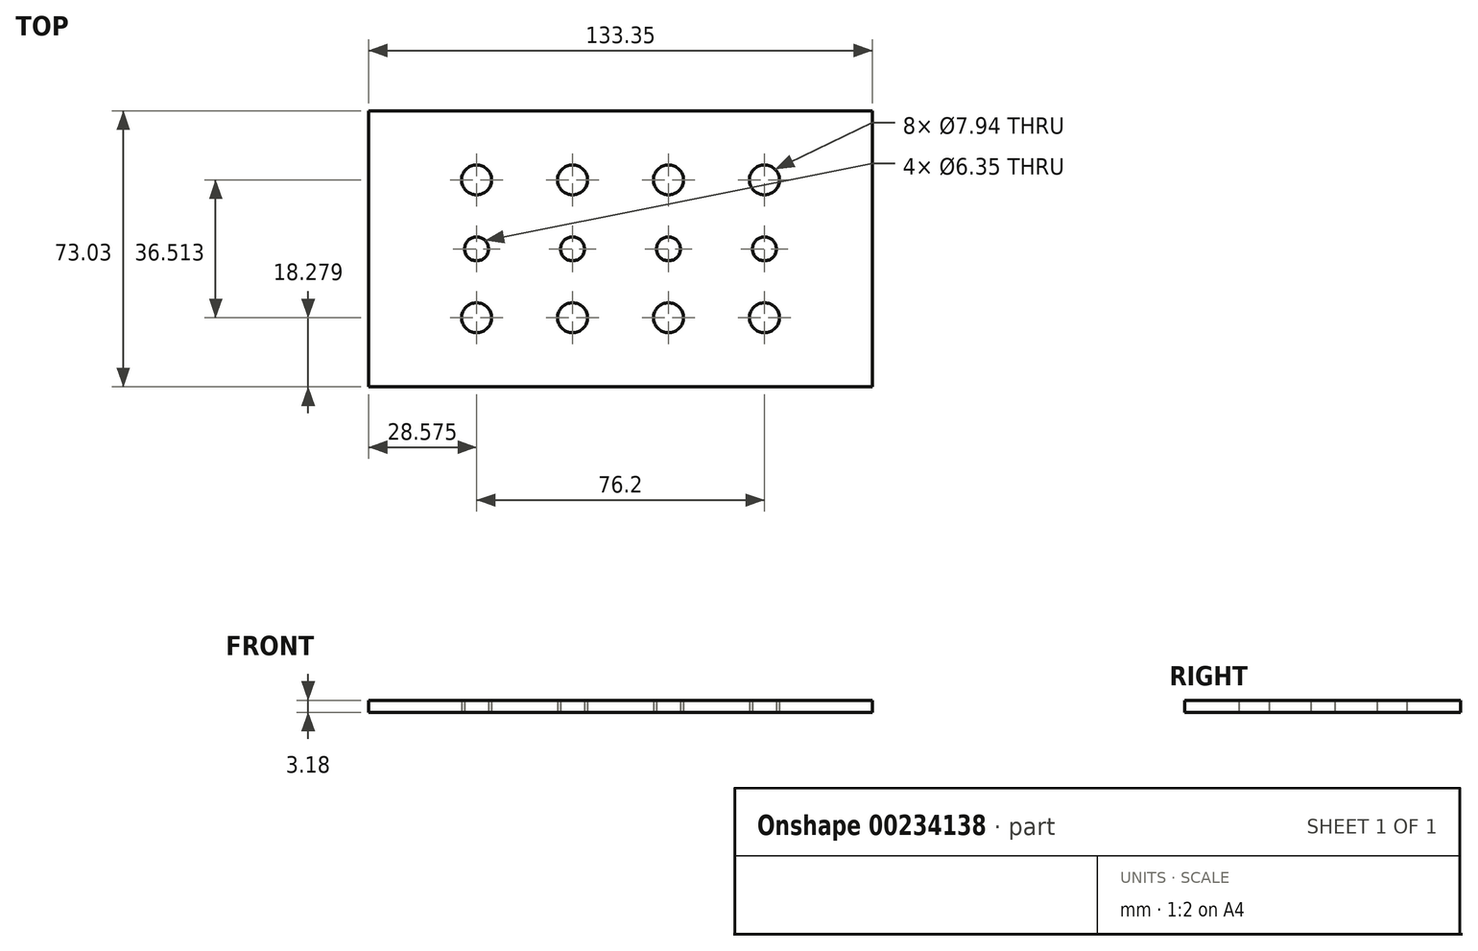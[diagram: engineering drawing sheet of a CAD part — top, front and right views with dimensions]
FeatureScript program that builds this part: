
annotation { "Feature Type Name" : "Feature", "Feature Type Description" : "" }
export const myFeature = defineFeature(function(context is Context, id is Id, definition is map)
    precondition{}
    {
        {
            var Q0;
            Q0=qCreatedBy(makeId("Top.planeOp"),FACE);
            var sketch = newSketch(context, id + "F0", { "sketchPlane" : qUnion([Q0])});
            skLineSegment(sketch, "E0.bottom", {"start": v(0, 0) * mm, "end": v(133.35, 0) * mm});
            skLineSegment(sketch, "E0.top", {"start": v(0, 73.03) * mm, "end": v(133.35, 73.03) * mm});
            skLineSegment(sketch, "E0.left", {"start": v(0, 0) * mm, "end": v(0, 73.03) * mm});
            skLineSegment(sketch, "E0.right", {"start": v(133.35, 0) * mm, "end": v(133.35, 73.03) * mm});
            skSolve(sketch);
        }
        {
            var Q0;
            Q0=makeQuery(id+"F0.imprint","IMPRINT",FACE,{"disambiguationData":[TD([[makeQuery(id+"F0.imprint","IMPRINT",EDGE,{"derivedFrom":sQuery(id+"F0.wireOp",EDGE,"E0.bottom")}),1.0]])]});
            extrude(context, id + "F1", {"entities" : qUnion([Q0]), "oppositeDirection" : true, "depth" : 3.17 * mm});
        }
        {
            var Q0;
            Q0=makeQuery(id+"F1.opExtrude","CAP_FACE",FACE,{"disambiguationData":[OSD([sQuery(id+"F0.wireOp",EDGE,"E0.bottom"),sQuery(id+"F0.wireOp",EDGE,"E0.top"),sQuery(id+"F0.wireOp",EDGE,"E0.left"),sQuery(id+"F0.wireOp",EDGE,"E0.right")])],"isStart":false});
            var sketch = newSketch(context, id + "F2", { "sketchPlane" : qUnion([Q0])});
            skLineSegment(sketch, "E1", {"start": v(0, -36.51) * mm, "end": v(133.35, -36.51) * mm, "construction": true});
            skCircle(sketch, "E2", {"center": v(28.58, -36.51) * mm, "radius": 3.18 * mm});
            skCircle(sketch, "E3.1.0.0", {"center": v(53.98, -36.51) * mm, "radius": 3.18 * mm});
            skCircle(sketch, "E3.2.0.0", {"center": v(79.38, -36.51) * mm, "radius": 3.18 * mm});
            skCircle(sketch, "E3.3.0.0", {"center": v(104.77, -36.51) * mm, "radius": 3.18 * mm});
            skLineSegment(sketch, "E3.direction1", {"start": v(28.58, -36.51) * mm, "end": v(53.98, -36.51) * mm, "construction": true});
            skSolve(sketch);
        }
        {
            var Q0;
            Q0=makeQuery(id+"F2.imprint","IMPRINT",FACE,{"disambiguationData":[TD([[makeQuery(id+"F2.imprint","IMPRINT",EDGE,{"derivedFrom":sQuery(id+"F2.wireOp",EDGE,"E2")}),1.0]])]});
            var Q1;
            Q1=makeQuery(id+"F2.imprint","IMPRINT",FACE,{"disambiguationData":[TD([[makeQuery(id+"F2.imprint","IMPRINT",EDGE,{"derivedFrom":sQuery(id+"F2.wireOp",EDGE,"E3.1.0.0")}),1.0]])]});
            var Q2;
            Q2=makeQuery(id+"F2.imprint","IMPRINT",FACE,{"disambiguationData":[TD([[makeQuery(id+"F2.imprint","IMPRINT",EDGE,{"derivedFrom":sQuery(id+"F2.wireOp",EDGE,"E3.2.0.0")}),1.0]])]});
            var Q3;
            Q3=makeQuery(id+"F2.imprint","IMPRINT",FACE,{"disambiguationData":[TD([[makeQuery(id+"F2.imprint","IMPRINT",EDGE,{"derivedFrom":sQuery(id+"F2.wireOp",EDGE,"E3.3.0.0")}),1.0]])]});
            extrude(context, id + "F3", {"entities" : qUnion([Q0, Q1, Q2, Q3]), "operationType" : NewBodyOperationType.REMOVE, "endBound" : BoundingType.THROUGH_ALL, "oppositeDirection" : true, "depth" : 25.4 * mm});
        }
        {
            var Q0;
            Q0=makeQuery(id+"F1.opExtrude","CAP_FACE",FACE,{"disambiguationData":[OSD([sQuery(id+"F0.wireOp",EDGE,"E0.bottom"),sQuery(id+"F0.wireOp",EDGE,"E0.top"),sQuery(id+"F0.wireOp",EDGE,"E0.left"),sQuery(id+"F0.wireOp",EDGE,"E0.right")])],"isStart":false});
            var sketch = newSketch(context, id + "F4", { "sketchPlane" : qUnion([Q0])});
            skLineSegment(sketch, "E4", {"start": v(0, -54.8) * mm, "end": v(125.38, -54.8) * mm, "construction": true});
            skCircle(sketch, "E5", {"center": v(28.58, -54.8) * mm, "radius": 3.97 * mm});
            skCircle(sketch, "E6.0.1.0", {"center": v(28.58, -18.28) * mm, "radius": 3.97 * mm});
            skCircle(sketch, "E6.1.0.0", {"center": v(53.98, -54.8) * mm, "radius": 3.97 * mm});
            skCircle(sketch, "E6.1.1.0", {"center": v(53.98, -18.28) * mm, "radius": 3.97 * mm});
            skCircle(sketch, "E6.2.0.0", {"center": v(79.38, -54.8) * mm, "radius": 3.97 * mm});
            skCircle(sketch, "E6.2.1.0", {"center": v(79.38, -18.28) * mm, "radius": 3.97 * mm});
            skCircle(sketch, "E6.3.0.0", {"center": v(104.77, -54.8) * mm, "radius": 3.97 * mm});
            skCircle(sketch, "E6.3.1.0", {"center": v(104.77, -18.28) * mm, "radius": 3.97 * mm});
            skLineSegment(sketch, "E6.direction1", {"start": v(28.58, -54.8) * mm, "end": v(53.98, -54.8) * mm, "construction": true});
            skLineSegment(sketch, "E6.direction2", {"start": v(28.58, -54.8) * mm, "end": v(28.58, -18.28) * mm, "construction": true});
            skSolve(sketch);
        }
        {
            var Q0;
            Q0=makeQuery(id+"F4.imprint","IMPRINT",FACE,{"disambiguationData":[TD([[makeQuery(id+"F4.imprint","IMPRINT",EDGE,{"derivedFrom":sQuery(id+"F4.wireOp",EDGE,"E5")}),1.0]])]});
            var Q1;
            Q1=makeQuery(id+"F4.imprint","IMPRINT",FACE,{"disambiguationData":[TD([[makeQuery(id+"F4.imprint","IMPRINT",EDGE,{"derivedFrom":sQuery(id+"F4.wireOp",EDGE,"E6.1.0.0")}),1.0]])]});
            var Q2;
            Q2=makeQuery(id+"F4.imprint","IMPRINT",FACE,{"disambiguationData":[TD([[makeQuery(id+"F4.imprint","IMPRINT",EDGE,{"derivedFrom":sQuery(id+"F4.wireOp",EDGE,"E6.2.0.0")}),1.0]])]});
            var Q3;
            Q3=makeQuery(id+"F4.imprint","IMPRINT",FACE,{"disambiguationData":[TD([[makeQuery(id+"F4.imprint","IMPRINT",EDGE,{"derivedFrom":sQuery(id+"F4.wireOp",EDGE,"E6.3.0.0")}),1.0]])]});
            var Q4;
            Q4=makeQuery(id+"F4.imprint","IMPRINT",FACE,{"disambiguationData":[TD([[makeQuery(id+"F4.imprint","IMPRINT",EDGE,{"derivedFrom":sQuery(id+"F4.wireOp",EDGE,"E6.3.1.0")}),1.0]])]});
            var Q5;
            Q5=makeQuery(id+"F4.imprint","IMPRINT",FACE,{"disambiguationData":[TD([[makeQuery(id+"F4.imprint","IMPRINT",EDGE,{"derivedFrom":sQuery(id+"F4.wireOp",EDGE,"E6.2.1.0")}),1.0]])]});
            var Q6;
            Q6=makeQuery(id+"F4.imprint","IMPRINT",FACE,{"disambiguationData":[TD([[makeQuery(id+"F4.imprint","IMPRINT",EDGE,{"derivedFrom":sQuery(id+"F4.wireOp",EDGE,"E6.1.1.0")}),1.0]])]});
            var Q7;
            Q7=makeQuery(id+"F4.imprint","IMPRINT",FACE,{"disambiguationData":[TD([[makeQuery(id+"F4.imprint","IMPRINT",EDGE,{"derivedFrom":sQuery(id+"F4.wireOp",EDGE,"E6.0.1.0")}),1.0]])]});
            extrude(context, id + "F5", {"entities" : qUnion([Q0, Q1, Q2, Q3, Q4, Q5, Q6, Q7]), "operationType" : NewBodyOperationType.REMOVE, "endBound" : BoundingType.THROUGH_ALL, "oppositeDirection" : true, "depth" : 25.4 * mm});
        }
    });
